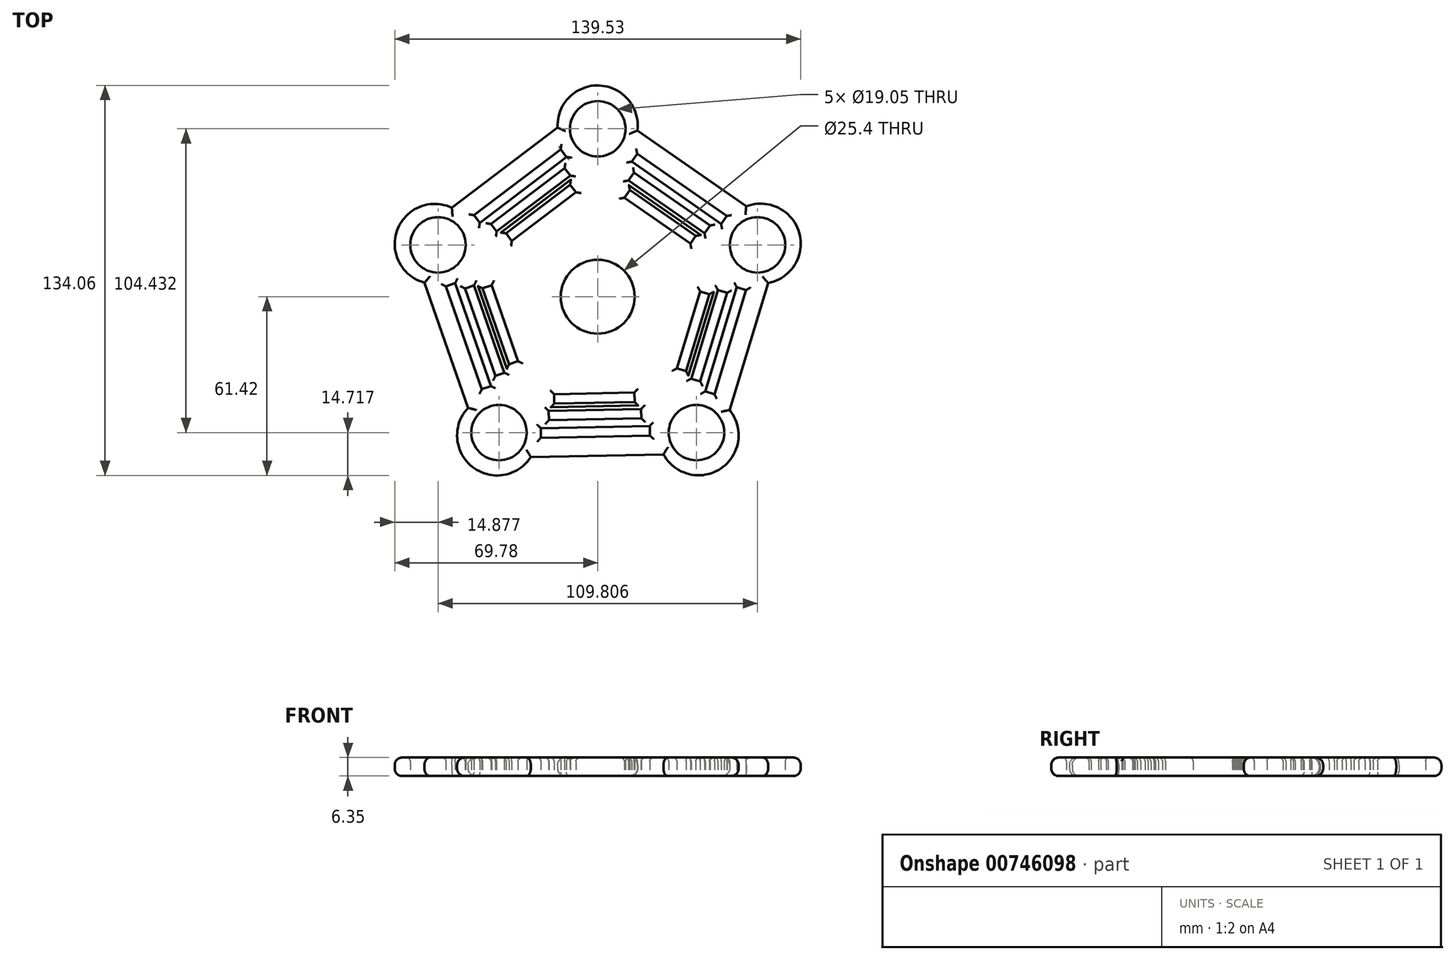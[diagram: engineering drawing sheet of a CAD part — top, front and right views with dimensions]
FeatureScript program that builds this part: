
annotation { "Feature Type Name" : "Feature", "Feature Type Description" : "" }
export const myFeature = defineFeature(function(context is Context, id is Id, definition is map)
    precondition{}
    {
        {
            var Q0;
            Q0=qCreatedBy(makeId("Top.planeOp"),FACE);
            var sketch = newSketch(context, id + "F0", { "sketchPlane" : qUnion([Q0])});
            skCircle(sketch, "E0", {"center": v(0, 0) * mm, "radius": 12.7 * mm});
            skCircle(sketch, "E1", {"center": v(0, 57.73) * mm, "radius": 9.53 * mm});
            skCircle(sketch, "E2.1.0", {"center": v(-54.9, 17.84) * mm, "radius": 9.53 * mm});
            skCircle(sketch, "E2.2.0", {"center": v(-33.93, -46.7) * mm, "radius": 9.53 * mm});
            skCircle(sketch, "E2.3.0", {"center": v(33.93, -46.7) * mm, "radius": 9.53 * mm});
            skCircle(sketch, "E2.4.0", {"center": v(54.9, 17.84) * mm, "radius": 9.53 * mm});
            skArc(sketch, "E3", {"start": v(13.6, 57.14) * mm, "mid": v(0.46, 72.63) * mm, "end": v(-13.79, 58.14) * mm});
            skArc(sketch, "E4.1.0", {"start": v(-50.14, 30.6) * mm, "mid": v(-68.94, 22.88) * mm, "end": v(-59.55, 4.85) * mm});
            skArc(sketch, "E4.2.0", {"start": v(-44.6, -38.23) * mm, "mid": v(-43.06, -58.5) * mm, "end": v(-23.02, -55.14) * mm});
            skArc(sketch, "E4.3.0", {"start": v(22.58, -54.22) * mm, "mid": v(42.33, -59.03) * mm, "end": v(45.32, -38.93) * mm});
            skArc(sketch, "E4.4.0", {"start": v(58.55, 4.72) * mm, "mid": v(69.22, 22.01) * mm, "end": v(51.03, 31.08) * mm});
            skLineSegment(sketch, "E5", {"start": v(-50.14, 30.6) * mm, "end": v(-13.79, 58.14) * mm});
            skLineSegment(sketch, "E6.1.0", {"start": v(-44.6, -38.23) * mm, "end": v(-59.55, 4.85) * mm});
            skLineSegment(sketch, "E6.2.0", {"start": v(22.58, -54.22) * mm, "end": v(-23.02, -55.14) * mm});
            skLineSegment(sketch, "E6.3.0", {"start": v(58.55, 4.72) * mm, "end": v(45.32, -38.93) * mm});
            skLineSegment(sketch, "E6.4.0", {"start": v(13.6, 57.14) * mm, "end": v(51.03, 31.08) * mm});
            skLineSegment(sketch, "E7", {"start": v(-42.56, 28.07) * mm, "end": v(-12.72, 50.68) * mm});
            skLineSegment(sketch, "E8", {"start": v(-42.56, 28.07) * mm, "end": v(-40.57, 25.44) * mm});
            skLineSegment(sketch, "E9", {"start": v(-12.72, 50.68) * mm, "end": v(-10.73, 48.05) * mm});
            skLineSegment(sketch, "E10", {"start": v(-40.57, 25.44) * mm, "end": v(-10.73, 48.05) * mm});
            skLineSegment(sketch, "E11", {"start": v(-36.72, 25.03) * mm, "end": v(-11.38, 44.23) * mm});
            skLineSegment(sketch, "E12", {"start": v(-36.72, 25.03) * mm, "end": v(-34.74, 22.43) * mm});
            skLineSegment(sketch, "E13", {"start": v(-11.38, 44.23) * mm, "end": v(-9.4, 41.63) * mm});
            skLineSegment(sketch, "E14", {"start": v(-34.74, 22.43) * mm, "end": v(-9.4, 41.63) * mm});
            skLineSegment(sketch, "E15.1.0", {"start": v(-39.85, -31.8) * mm, "end": v(-52.13, 3.56) * mm});
            skLineSegment(sketch, "E15.1.1", {"start": v(-52.13, 3.56) * mm, "end": v(-49.01, 4.64) * mm});
            skLineSegment(sketch, "E15.1.2", {"start": v(-36.73, -30.72) * mm, "end": v(-49.01, 4.64) * mm});
            skLineSegment(sketch, "E15.1.3", {"start": v(-39.85, -31.8) * mm, "end": v(-36.73, -30.72) * mm});
            skLineSegment(sketch, "E15.2.0", {"start": v(17.93, -47.72) * mm, "end": v(-19.5, -48.48) * mm});
            skLineSegment(sketch, "E15.2.1", {"start": v(-19.5, -48.48) * mm, "end": v(-19.56, -45.18) * mm});
            skLineSegment(sketch, "E15.2.2", {"start": v(17.87, -44.42) * mm, "end": v(-19.56, -45.18) * mm});
            skLineSegment(sketch, "E15.2.3", {"start": v(17.93, -47.72) * mm, "end": v(17.87, -44.42) * mm});
            skLineSegment(sketch, "E15.3.0", {"start": v(50.93, 2.3) * mm, "end": v(40.08, -33.52) * mm});
            skLineSegment(sketch, "E15.3.1", {"start": v(40.08, -33.52) * mm, "end": v(36.92, -32.57) * mm});
            skLineSegment(sketch, "E15.3.2", {"start": v(47.77, 3.26) * mm, "end": v(36.92, -32.57) * mm});
            skLineSegment(sketch, "E15.3.3", {"start": v(50.93, 2.3) * mm, "end": v(47.77, 3.26) * mm});
            skLineSegment(sketch, "E15.4.0", {"start": v(13.54, 49.15) * mm, "end": v(44.27, 27.76) * mm});
            skLineSegment(sketch, "E15.4.1", {"start": v(44.27, 27.76) * mm, "end": v(42.38, 25.05) * mm});
            skLineSegment(sketch, "E15.4.2", {"start": v(11.66, 46.44) * mm, "end": v(42.38, 25.05) * mm});
            skLineSegment(sketch, "E15.4.3", {"start": v(13.54, 49.15) * mm, "end": v(11.66, 46.44) * mm});
            skLineSegment(sketch, "E16.1.0", {"start": v(-35.15, -27.18) * mm, "end": v(-32.07, -26.11) * mm});
            skLineSegment(sketch, "E16.1.1", {"start": v(-35.15, -27.18) * mm, "end": v(-45.58, 2.85) * mm});
            skLineSegment(sketch, "E16.1.2", {"start": v(-32.07, -26.11) * mm, "end": v(-42.5, 3.92) * mm});
            skLineSegment(sketch, "E16.1.3", {"start": v(-45.58, 2.85) * mm, "end": v(-42.5, 3.92) * mm});
            skLineSegment(sketch, "E16.2.0", {"start": v(15, -41.83) * mm, "end": v(14.93, -38.57) * mm});
            skLineSegment(sketch, "E16.2.1", {"start": v(15, -41.83) * mm, "end": v(-16.8, -42.47) * mm});
            skLineSegment(sketch, "E16.2.2", {"start": v(14.93, -38.57) * mm, "end": v(-16.86, -39.2) * mm});
            skLineSegment(sketch, "E16.2.3", {"start": v(-16.8, -42.47) * mm, "end": v(-16.86, -39.2) * mm});
            skLineSegment(sketch, "E16.3.0", {"start": v(44.42, 1.33) * mm, "end": v(41.3, 2.28) * mm});
            skLineSegment(sketch, "E16.3.1", {"start": v(44.42, 1.33) * mm, "end": v(35.2, -29.1) * mm});
            skLineSegment(sketch, "E16.3.2", {"start": v(41.3, 2.28) * mm, "end": v(32.08, -28.15) * mm});
            skLineSegment(sketch, "E16.3.3", {"start": v(35.2, -29.1) * mm, "end": v(32.08, -28.15) * mm});
            skLineSegment(sketch, "E16.4.0", {"start": v(12.46, 42.65) * mm, "end": v(10.6, 39.97) * mm});
            skLineSegment(sketch, "E16.4.1", {"start": v(12.46, 42.65) * mm, "end": v(38.55, 24.49) * mm});
            skLineSegment(sketch, "E16.4.2", {"start": v(10.6, 39.97) * mm, "end": v(36.69, 21.8) * mm});
            skLineSegment(sketch, "E16.4.3", {"start": v(38.55, 24.49) * mm, "end": v(36.69, 21.8) * mm});
            skLineSegment(sketch, "E17", {"start": v(-31.5, 21.83) * mm, "end": v(-9.5, 38.5) * mm});
            skLineSegment(sketch, "E18", {"start": v(-31.5, 21.83) * mm, "end": v(-29.53, 19.22) * mm});
            skLineSegment(sketch, "E19", {"start": v(-9.5, 38.5) * mm, "end": v(-7.52, 35.9) * mm});
            skLineSegment(sketch, "E20", {"start": v(-29.53, 19.22) * mm, "end": v(-7.52, 35.9) * mm});
            skLineSegment(sketch, "E21.1.0", {"start": v(-30.5, -23.22) * mm, "end": v(-39.56, 2.87) * mm});
            skLineSegment(sketch, "E21.1.1", {"start": v(-27.4, -22.15) * mm, "end": v(-36.47, 3.94) * mm});
            skLineSegment(sketch, "E21.1.2", {"start": v(-39.56, 2.87) * mm, "end": v(-36.47, 3.94) * mm});
            skLineSegment(sketch, "E21.1.3", {"start": v(-30.5, -23.22) * mm, "end": v(-27.4, -22.15) * mm});
            skLineSegment(sketch, "E21.2.0", {"start": v(12.66, -36.18) * mm, "end": v(-14.95, -36.73) * mm});
            skLineSegment(sketch, "E21.2.1", {"start": v(12.6, -32.91) * mm, "end": v(-15.02, -33.47) * mm});
            skLineSegment(sketch, "E21.2.2", {"start": v(-14.95, -36.73) * mm, "end": v(-15.02, -33.47) * mm});
            skLineSegment(sketch, "E21.2.3", {"start": v(12.66, -36.18) * mm, "end": v(12.6, -32.91) * mm});
            skLineSegment(sketch, "E21.3.0", {"start": v(38.32, 0.86) * mm, "end": v(30.32, -25.57) * mm});
            skLineSegment(sketch, "E21.3.1", {"start": v(35.2, 1.8) * mm, "end": v(27.2, -24.63) * mm});
            skLineSegment(sketch, "E21.3.2", {"start": v(30.32, -25.57) * mm, "end": v(27.2, -24.63) * mm});
            skLineSegment(sketch, "E21.3.3", {"start": v(38.32, 0.86) * mm, "end": v(35.2, 1.8) * mm});
            skLineSegment(sketch, "E21.4.0", {"start": v(11.02, 36.7) * mm, "end": v(33.7, 20.93) * mm});
            skLineSegment(sketch, "E21.4.1", {"start": v(9.16, 34.03) * mm, "end": v(31.83, 18.25) * mm});
            skLineSegment(sketch, "E21.4.2", {"start": v(33.7, 20.93) * mm, "end": v(31.83, 18.25) * mm});
            skLineSegment(sketch, "E21.4.3", {"start": v(11.02, 36.7) * mm, "end": v(9.16, 34.03) * mm});
            skSolve(sketch);
        }
        {
            var Q0;
            Q0=makeQuery(id+"F0.imprint","IMPRINT",FACE,{"disambiguationData":[TD([[makeQuery(id+"F0.imprint","IMPRINT",EDGE,{"derivedFrom":sQuery(id+"F0.wireOp",EDGE,"E0")}),-1.0]])]});
            extrude(context, id + "F1", {"entities" : qUnion([Q0]), "depth" : 6.35 * mm, "offsetDistance" : 25.4 * mm});
        }
        {
            var Q0;
            Q0=makeQuery(id+"F1.opExtrude","CAP_EDGE",EDGE,{"disambiguationData":[OSD([sQuery(id+"F0.wireOp",EDGE,"E6.4.0")])],"isStart":true});
            var Q1;
            Q1=makeQuery(id+"F1.opExtrude","CAP_EDGE",EDGE,{"disambiguationData":[OSD([sQuery(id+"F0.wireOp",EDGE,"E4.4.0")])],"isStart":true});
            var Q2;
            Q2=makeQuery(id+"F1.opExtrude","CAP_EDGE",EDGE,{"disambiguationData":[OSD([sQuery(id+"F0.wireOp",EDGE,"E6.3.0")])],"isStart":true});
            var Q3;
            Q3=makeQuery(id+"F1.opExtrude","CAP_EDGE",EDGE,{"disambiguationData":[OSD([sQuery(id+"F0.wireOp",EDGE,"E6.2.0")])],"isStart":true});
            var Q4;
            Q4=makeQuery(id+"F1.opExtrude","CAP_EDGE",EDGE,{"disambiguationData":[OSD([sQuery(id+"F0.wireOp",EDGE,"E4.3.0")])],"isStart":true});
            var Q5;
            Q5=makeQuery(id+"F1.opExtrude","CAP_EDGE",EDGE,{"disambiguationData":[OSD([sQuery(id+"F0.wireOp",EDGE,"E4.3.0")])],"isStart":false});
            var Q6;
            Q6=makeQuery(id+"F1.opExtrude","CAP_EDGE",EDGE,{"disambiguationData":[OSD([sQuery(id+"F0.wireOp",EDGE,"E6.3.0")])],"isStart":false});
            var Q7;
            Q7=makeQuery(id+"F1.opExtrude","CAP_EDGE",EDGE,{"disambiguationData":[OSD([sQuery(id+"F0.wireOp",EDGE,"E6.4.0")])],"isStart":false});
            var Q8;
            Q8=makeQuery(id+"F1.opExtrude","CAP_EDGE",EDGE,{"disambiguationData":[OSD([sQuery(id+"F0.wireOp",EDGE,"E4.4.0")])],"isStart":false});
            var Q9;
            Q9=makeQuery(id+"F1.opExtrude","CAP_EDGE",EDGE,{"disambiguationData":[OSD([sQuery(id+"F0.wireOp",EDGE,"E4.2.0")])],"isStart":true});
            var Q10;
            Q10=makeQuery(id+"F1.opExtrude","CAP_EDGE",EDGE,{"disambiguationData":[OSD([sQuery(id+"F0.wireOp",EDGE,"E6.1.0")])],"isStart":true});
            var Q11;
            Q11=makeQuery(id+"F1.opExtrude","CAP_EDGE",EDGE,{"disambiguationData":[OSD([sQuery(id+"F0.wireOp",EDGE,"E3")])],"isStart":true});
            var Q12;
            Q12=makeQuery(id+"F1.opExtrude","CAP_EDGE",EDGE,{"disambiguationData":[OSD([sQuery(id+"F0.wireOp",EDGE,"E3")])],"isStart":false});
            var Q13;
            Q13=makeQuery(id+"F1.opExtrude","CAP_EDGE",EDGE,{"disambiguationData":[OSD([sQuery(id+"F0.wireOp",EDGE,"E6.2.0")])],"isStart":false});
            var Q14;
            Q14=makeQuery(id+"F1.opExtrude","CAP_EDGE",EDGE,{"disambiguationData":[OSD([sQuery(id+"F0.wireOp",EDGE,"E4.2.0")])],"isStart":false});
            var Q15;
            Q15=makeQuery(id+"F1.opExtrude","CAP_EDGE",EDGE,{"disambiguationData":[OSD([sQuery(id+"F0.wireOp",EDGE,"E5")])],"isStart":false});
            var Q16;
            Q16=makeQuery(id+"F1.opExtrude","CAP_EDGE",EDGE,{"disambiguationData":[OSD([sQuery(id+"F0.wireOp",EDGE,"E6.1.0")])],"isStart":false});
            var Q17;
            Q17=makeQuery(id+"F1.opExtrude","CAP_EDGE",EDGE,{"disambiguationData":[OSD([sQuery(id+"F0.wireOp",EDGE,"E4.1.0")])],"isStart":false});
            var Q18;
            Q18=makeQuery(id+"F1.opExtrude","CAP_EDGE",EDGE,{"disambiguationData":[OSD([sQuery(id+"F0.wireOp",EDGE,"E4.1.0")])],"isStart":true});
            var Q19;
            Q19=makeQuery(id+"F1.opExtrude","CAP_EDGE",EDGE,{"disambiguationData":[OSD([sQuery(id+"F0.wireOp",EDGE,"E5")])],"isStart":true});
            fillet(context, id + "F2", {"entities" : qUnion([Q0, Q1, Q2, Q3, Q4, Q5, Q6, Q7, Q8, Q9, Q10, Q11, Q12, Q13, Q14, Q15, Q16, Q17, Q18, Q19]), "radius" : 2.54 * mm, "tangentPropagation" : true, "allowEdgeOverflow" : false});
        }
        {
            var Q0;
            Q0=makeQuery(id+"F1.opExtrude","CAP_EDGE",EDGE,{"disambiguationData":[OSD([sQuery(id+"F0.wireOp",EDGE,"E7")])],"isStart":false});
            var Q1;
            Q1=makeQuery(id+"F1.opExtrude","CAP_EDGE",EDGE,{"disambiguationData":[OSD([sQuery(id+"F0.wireOp",EDGE,"E7")])],"isStart":true});
            var Q2;
            Q2=makeQuery(id+"F1.opExtrude","CAP_EDGE",EDGE,{"disambiguationData":[OSD([sQuery(id+"F0.wireOp",EDGE,"E8")])],"isStart":false});
            var Q3;
            Q3=makeQuery(id+"F1.opExtrude","CAP_EDGE",EDGE,{"disambiguationData":[OSD([sQuery(id+"F0.wireOp",EDGE,"E8")])],"isStart":true});
            var Q4;
            Q4=makeQuery(id+"F1.opExtrude","CAP_EDGE",EDGE,{"disambiguationData":[OSD([sQuery(id+"F0.wireOp",EDGE,"E10")])],"isStart":false});
            var Q5;
            Q5=makeQuery(id+"F1.opExtrude","CAP_EDGE",EDGE,{"disambiguationData":[OSD([sQuery(id+"F0.wireOp",EDGE,"E10")])],"isStart":true});
            var Q6;
            Q6=makeQuery(id+"F1.opExtrude","CAP_FACE",FACE,{"disambiguationData":[OSD([sQuery(id+"F0.wireOp",EDGE,"E0"),sQuery(id+"F0.wireOp",EDGE,"E1"),sQuery(id+"F0.wireOp",EDGE,"E2.1.0"),sQuery(id+"F0.wireOp",EDGE,"E2.2.0"),sQuery(id+"F0.wireOp",EDGE,"E2.3.0"),sQuery(id+"F0.wireOp",EDGE,"E2.4.0"),sQuery(id+"F0.wireOp",EDGE,"E3"),sQuery(id+"F0.wireOp",EDGE,"E4.1.0"),sQuery(id+"F0.wireOp",EDGE,"E4.2.0"),sQuery(id+"F0.wireOp",EDGE,"E4.3.0"),sQuery(id+"F0.wireOp",EDGE,"E4.4.0"),sQuery(id+"F0.wireOp",EDGE,"E5"),sQuery(id+"F0.wireOp",EDGE,"E6.1.0"),sQuery(id+"F0.wireOp",EDGE,"E6.2.0"),sQuery(id+"F0.wireOp",EDGE,"E6.3.0"),sQuery(id+"F0.wireOp",EDGE,"E6.4.0"),sQuery(id+"F0.wireOp",EDGE,"E7"),sQuery(id+"F0.wireOp",EDGE,"E8"),sQuery(id+"F0.wireOp",EDGE,"E9"),sQuery(id+"F0.wireOp",EDGE,"E10"),sQuery(id+"F0.wireOp",EDGE,"E11"),sQuery(id+"F0.wireOp",EDGE,"E12"),sQuery(id+"F0.wireOp",EDGE,"E13"),sQuery(id+"F0.wireOp",EDGE,"E14"),sQuery(id+"F0.wireOp",EDGE,"E15.1.0"),sQuery(id+"F0.wireOp",EDGE,"E15.1.1"),sQuery(id+"F0.wireOp",EDGE,"E15.1.2"),sQuery(id+"F0.wireOp",EDGE,"E15.1.3"),sQuery(id+"F0.wireOp",EDGE,"E15.2.0"),sQuery(id+"F0.wireOp",EDGE,"E15.2.1"),sQuery(id+"F0.wireOp",EDGE,"E15.2.2"),sQuery(id+"F0.wireOp",EDGE,"E15.2.3"),sQuery(id+"F0.wireOp",EDGE,"E15.3.0"),sQuery(id+"F0.wireOp",EDGE,"E15.3.1"),sQuery(id+"F0.wireOp",EDGE,"E15.3.2"),sQuery(id+"F0.wireOp",EDGE,"E15.3.3"),sQuery(id+"F0.wireOp",EDGE,"E15.4.0"),sQuery(id+"F0.wireOp",EDGE,"E15.4.1"),sQuery(id+"F0.wireOp",EDGE,"E15.4.2"),sQuery(id+"F0.wireOp",EDGE,"E15.4.3"),sQuery(id+"F0.wireOp",EDGE,"E16.1.0"),sQuery(id+"F0.wireOp",EDGE,"E16.1.1"),sQuery(id+"F0.wireOp",EDGE,"E16.1.2"),sQuery(id+"F0.wireOp",EDGE,"E16.1.3"),sQuery(id+"F0.wireOp",EDGE,"E16.2.0"),sQuery(id+"F0.wireOp",EDGE,"E16.2.1"),sQuery(id+"F0.wireOp",EDGE,"E16.2.2"),sQuery(id+"F0.wireOp",EDGE,"E16.2.3"),sQuery(id+"F0.wireOp",EDGE,"E16.3.0"),sQuery(id+"F0.wireOp",EDGE,"E16.3.1"),sQuery(id+"F0.wireOp",EDGE,"E16.3.2"),sQuery(id+"F0.wireOp",EDGE,"E16.3.3"),sQuery(id+"F0.wireOp",EDGE,"E16.4.0"),sQuery(id+"F0.wireOp",EDGE,"E16.4.1"),sQuery(id+"F0.wireOp",EDGE,"E16.4.2"),sQuery(id+"F0.wireOp",EDGE,"E16.4.3"),sQuery(id+"F0.wireOp",EDGE,"E17"),sQuery(id+"F0.wireOp",EDGE,"E18"),sQuery(id+"F0.wireOp",EDGE,"E19"),sQuery(id+"F0.wireOp",EDGE,"E20"),sQuery(id+"F0.wireOp",EDGE,"E21.1.0"),sQuery(id+"F0.wireOp",EDGE,"E21.1.1"),sQuery(id+"F0.wireOp",EDGE,"E21.1.2"),sQuery(id+"F0.wireOp",EDGE,"E21.1.3"),sQuery(id+"F0.wireOp",EDGE,"E21.2.0"),sQuery(id+"F0.wireOp",EDGE,"E21.2.1"),sQuery(id+"F0.wireOp",EDGE,"E21.2.2"),sQuery(id+"F0.wireOp",EDGE,"E21.2.3"),sQuery(id+"F0.wireOp",EDGE,"E21.3.0"),sQuery(id+"F0.wireOp",EDGE,"E21.3.1"),sQuery(id+"F0.wireOp",EDGE,"E21.3.2"),sQuery(id+"F0.wireOp",EDGE,"E21.3.3"),sQuery(id+"F0.wireOp",EDGE,"E21.4.0"),sQuery(id+"F0.wireOp",EDGE,"E21.4.1"),sQuery(id+"F0.wireOp",EDGE,"E21.4.2"),sQuery(id+"F0.wireOp",EDGE,"E21.4.3")])],"isStart":false});
            fillet(context, id + "F3", {"entities" : qUnion([Q0, Q1, Q2, Q3, Q4, Q5, Q6]), "radius" : 1.27 * mm, "tangentPropagation" : true, "allowEdgeOverflow" : false});
        }
    });
